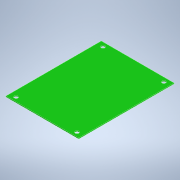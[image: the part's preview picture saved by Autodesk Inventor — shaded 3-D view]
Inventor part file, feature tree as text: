
AUTODESK INVENTOR PART (.ipt)
format: ipt  version: 2022 (Build 260153000, 153)  size: 3,077,632 bytes
history: native  units: in
note: dims shown in document units (in); Inventor stores cm internally (conversion verified against a paired STEP export)
features: extrude x2, sketch x2, hole x1
ambient origin geometry x8: Origin, YZ Plane, XZ Plane, XY Plane, X Axis, Y Axis, Z Axis, Center Point
bodies: Solid1 (feature_tree)
feature tree (5):
  extrude  "Extrusion1"  Depth=2.2244in
  hole  "Hole2"  [1 undecoded]
  extrude  "Extrusion4"  Depth=1.4213in
  sketch  "Sketch1"  dims[d0=1.6969in d1=2.2244in]
  sketch  "Sketch6"  dims[d2=0.0197in d3=0.0in d33=2.0276in d34=1.4213in d35=1.0138in d36=0.7106in d37=0.0866in d38=0.2726in d39=0.1732in d40=0.0787in d41=90.0deg d42=0.315in d43=0.8108in d57=0.0039in d58=0.0118in d59=0.128in d60=0.1535in d61=27.9528in d63=0.0098in d64=0.3937in d66=0.3937in d68=0.0118in d69=0.0039in d70=0.0049in d71=0.003in d72=27.9528in d74=0.0098in d75=0.3937in d77=0.3937in d79=0.002in d80=0.0in d81=0.7874in d83=0.8504in d84=0.3937in d86=0.3937in d88=0.7874in d90=360.0deg]
note: 1 required parameter value undecoded (feature->parameter linkage not recoverable at this tier; creation-order binding heuristic only, values carry confidence <= 0.55)
